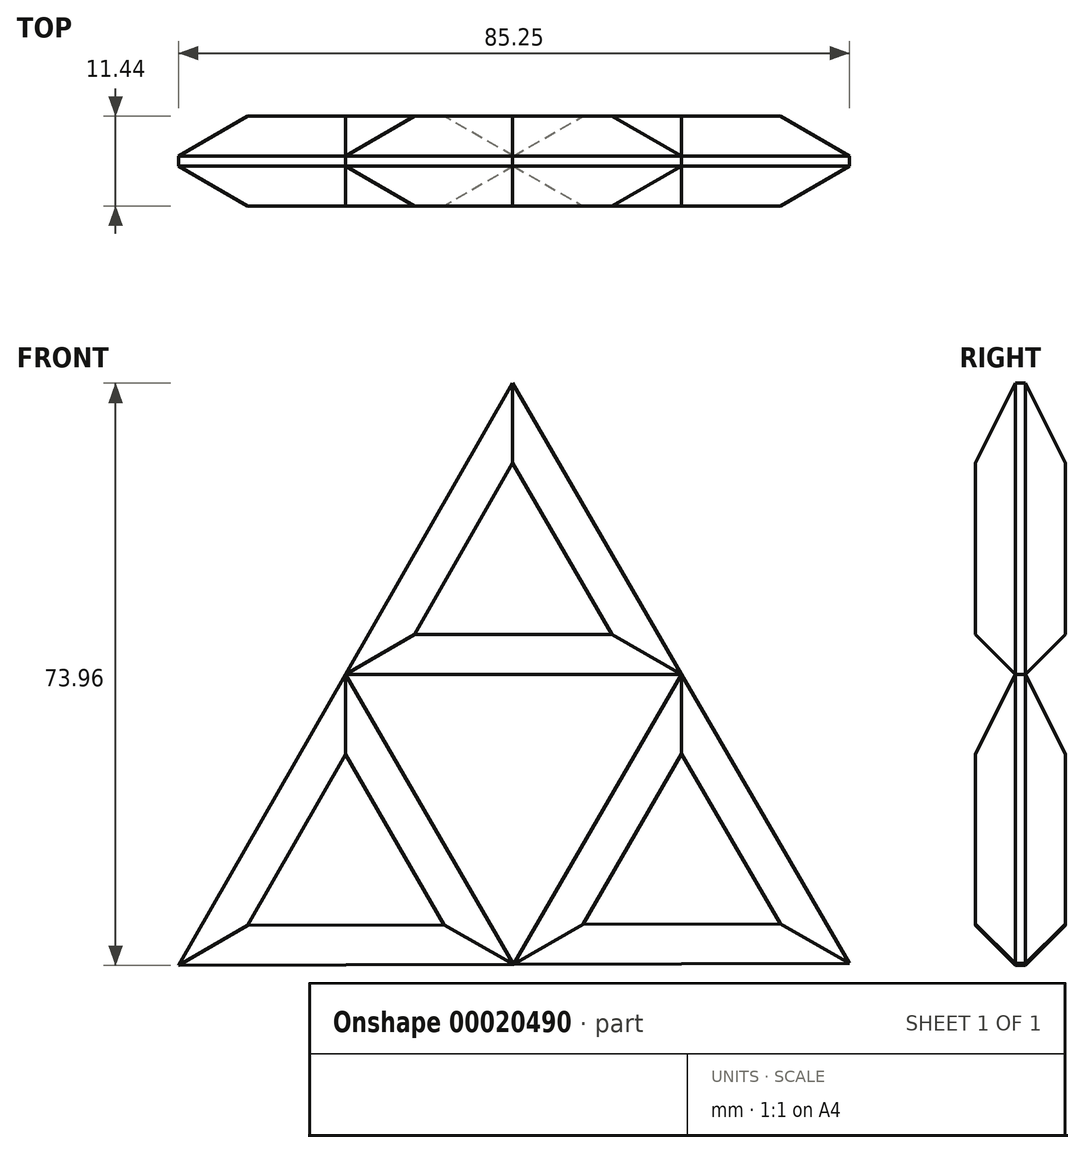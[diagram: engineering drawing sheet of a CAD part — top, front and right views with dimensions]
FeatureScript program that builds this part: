
annotation { "Feature Type Name" : "Feature", "Feature Type Description" : "" }
export const myFeature = defineFeature(function(context is Context, id is Id, definition is map)
    precondition{}
    {
        {
            var Q0;
            Q0=qCreatedBy(makeId("Front.planeOp"),FACE);
            var sketch = newSketch(context, id + "F0", { "sketchPlane" : qUnion([Q0])});
            skCircle(sketch, "E0.cCircle", {"center": v(0, 0) * mm, "radius": 24.6 * mm, "construction": true});
            skLineSegment(sketch, "E0.0", {"start": v(-42.55, -24.74) * mm, "end": v(-0.15, 49.22) * mm});
            skLineSegment(sketch, "E0.1", {"start": v(-0.15, 49.22) * mm, "end": v(42.7, -24.48) * mm});
            skLineSegment(sketch, "E0.2", {"start": v(42.7, -24.48) * mm, "end": v(-42.55, -24.74) * mm});
            skPoint(sketch, "E0.0.midPoint", {"position": v(-21.35, 12.24) * mm});
            skLineSegment(sketch, "E1", {"start": v(-21.35, 12.24) * mm, "end": v(0, -24.6) * mm});
            skLineSegment(sketch, "E2", {"start": v(-21.35, 12.24) * mm, "end": v(21.35, 12.24) * mm});
            skLineSegment(sketch, "E3", {"start": v(21.35, 12.24) * mm, "end": v(0, -24.6) * mm});
            skSolve(sketch);
        }
        {
            var Q0;
            {var subQ0=sQuery(id+"F0.wireOp",EDGE,"E2");Q0=makeQuery(id+"F0.imprint","IMPRINT",FACE,{"disambiguationData":[TD([[makeQuery(id+"F0.imprint","IMPRINT",EDGE,{"derivedFrom":subQ0}),1.0]])]});}
            var Q1;
            {var subQ0=sQuery(id+"F0.wireOp",EDGE,"E1");Q1=makeQuery(id+"F0.imprint","IMPRINT",FACE,{"disambiguationData":[TD([[makeQuery(id+"F0.imprint","IMPRINT",EDGE,{"derivedFrom":subQ0}),-1.0]])]});}
            var Q2;
            {var subQ0=sQuery(id+"F0.wireOp",EDGE,"E3");Q2=makeQuery(id+"F0.imprint","IMPRINT",FACE,{"disambiguationData":[TD([[makeQuery(id+"F0.imprint","IMPRINT",EDGE,{"derivedFrom":subQ0}),1.0]])]});}
            extrude(context, id + "F1", {"entities" : qUnion([Q0, Q1, Q2]), "endBound" : BoundingType.SYMMETRIC, "depth" : 6.35 * mm});
        }
        {
            var Q0;
            Q0=makeQuery(id+"F1.opExtrude","CAP_FACE",FACE,{"disambiguationData":[OSD([sQuery(id+"F0.wireOp",EDGE,"E0.0"),sQuery(id+"F0.wireOp",EDGE,"E0.1"),sQuery(id+"F0.wireOp",EDGE,"E2")])],"isStart":false});
            var Q1;
            Q1=makeQuery(id+"F1.opExtrude","CAP_FACE",FACE,{"disambiguationData":[OSD([sQuery(id+"F0.wireOp",EDGE,"E0.0"),sQuery(id+"F0.wireOp",EDGE,"E0.2"),sQuery(id+"F0.wireOp",EDGE,"E1")])],"isStart":false});
            var Q2;
            Q2=makeQuery(id+"F1.opExtrude","CAP_FACE",FACE,{"disambiguationData":[OSD([sQuery(id+"F0.wireOp",EDGE,"E0.1"),sQuery(id+"F0.wireOp",EDGE,"E0.2"),sQuery(id+"F0.wireOp",EDGE,"E3")])],"isStart":false});
            chamfer(context, id + "F2", {"entities" : qUnion([Q0, Q1, Q2]), "width" : 5.08 * mm, "tangentPropagation" : true});
        }
        {
            var Q0;
            Q0=makeQuery(id+"F1.opExtrude","CAP_FACE",FACE,{"disambiguationData":[OSD([sQuery(id+"F0.wireOp",EDGE,"E0.0"),sQuery(id+"F0.wireOp",EDGE,"E0.1"),sQuery(id+"F0.wireOp",EDGE,"E2")])],"isStart":true});
            var Q1;
            Q1=makeQuery(id+"F1.opExtrude","CAP_FACE",FACE,{"disambiguationData":[OSD([sQuery(id+"F0.wireOp",EDGE,"E0.1"),sQuery(id+"F0.wireOp",EDGE,"E0.2"),sQuery(id+"F0.wireOp",EDGE,"E3")])],"isStart":true});
            var Q2;
            Q2=makeQuery(id+"F1.opExtrude","CAP_FACE",FACE,{"disambiguationData":[OSD([sQuery(id+"F0.wireOp",EDGE,"E0.0"),sQuery(id+"F0.wireOp",EDGE,"E0.2"),sQuery(id+"F0.wireOp",EDGE,"E1")])],"isStart":true});
            extrude(context, id + "F3", {"entities" : qUnion([Q0, Q1, Q2]), "depth" : 5.08 * mm});
        }
        {
            var Q0;
            Q0=makeQuery(id+"F3.opExtrude","CAP_FACE",FACE,{"disambiguationData":[OSD([sQuery(id+"F0.wireOp",EDGE,"E0.0"),sQuery(id+"F0.wireOp",EDGE,"E0.1"),sQuery(id+"F0.wireOp",EDGE,"E2")])],"isStart":false});
            var Q1;
            Q1=makeQuery(id+"F3.opExtrude","CAP_FACE",FACE,{"disambiguationData":[OSD([sQuery(id+"F0.wireOp",EDGE,"E0.1"),sQuery(id+"F0.wireOp",EDGE,"E0.2"),sQuery(id+"F0.wireOp",EDGE,"E3")])],"isStart":false});
            var Q2;
            Q2=makeQuery(id+"F3.opExtrude","CAP_FACE",FACE,{"disambiguationData":[OSD([sQuery(id+"F0.wireOp",EDGE,"E0.0"),sQuery(id+"F0.wireOp",EDGE,"E0.2"),sQuery(id+"F0.wireOp",EDGE,"E1")])],"isStart":false});
            chamfer(context, id + "F4", {"entities" : qUnion([Q0, Q1, Q2]), "width" : 5.08 * mm, "tangentPropagation" : true});
        }
    });
